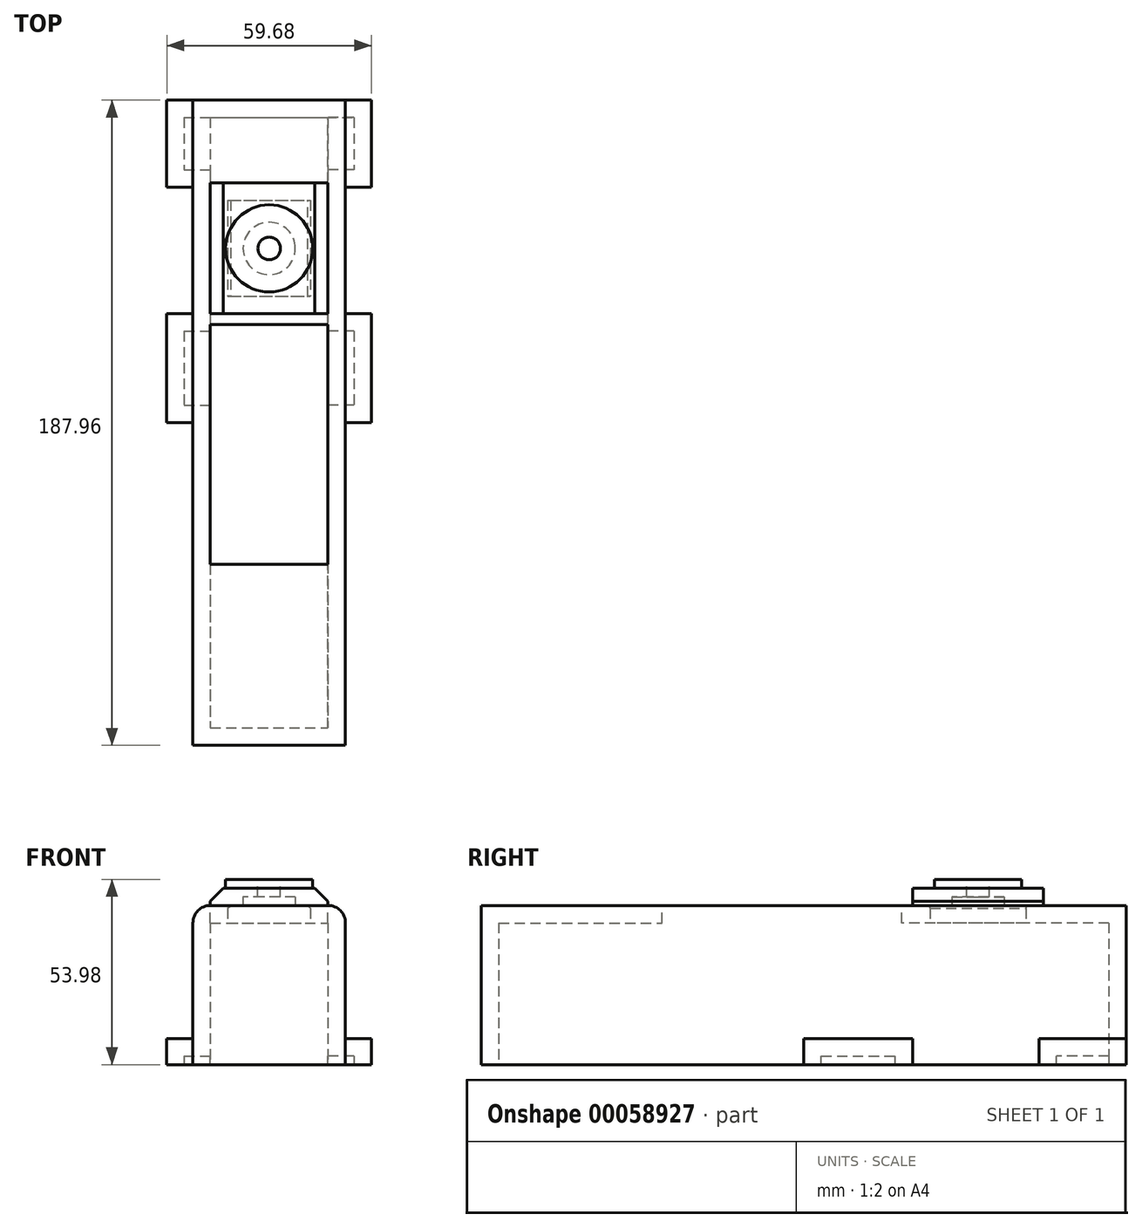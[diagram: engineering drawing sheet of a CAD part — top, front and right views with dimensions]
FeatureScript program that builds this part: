
annotation { "Feature Type Name" : "Feature", "Feature Type Description" : "" }
export const myFeature = defineFeature(function(context is Context, id is Id, definition is map)
    precondition{}
    {
        {
            var Q0;
            Q0=qCreatedBy(makeId("Top.planeOp"),FACE);
            var sketch = newSketch(context, id + "F0", { "sketchPlane" : qUnion([Q0])});
            skLineSegment(sketch, "E0.rect.bottom", {"start": v(-22.22, 93.98) * mm, "end": v(22.22, 93.98) * mm});
            skLineSegment(sketch, "E0.rect.top", {"start": v(-22.22, -93.98) * mm, "end": v(22.22, -93.98) * mm});
            skLineSegment(sketch, "E0.rect.left", {"start": v(-22.22, 93.98) * mm, "end": v(-22.22, -93.98) * mm});
            skLineSegment(sketch, "E0.rect.right", {"start": v(22.22, 93.98) * mm, "end": v(22.22, -93.98) * mm});
            skPoint(sketch, "E0.rect.middle", {"position": v(0, 0) * mm});
            skSolve(sketch);
        }
        {
            var Q0;
            Q0=makeQuery(id+"F0.imprint","IMPRINT",FACE,{"disambiguationData":[TD([[makeQuery(id+"F0.imprint","IMPRINT",EDGE,{"derivedFrom":sQuery(id+"F0.wireOp",EDGE,"E0.rect.bottom")}),-1.0]])]});
            extrude(context, id + "F1", {"entities" : qUnion([Q0]), "depth" : 46.35 * mm});
        }
        {
            var Q0;
            Q0=makeQuery(id+"F1.opExtrude","CAP_EDGE",EDGE,{"disambiguationData":[OSD([sQuery(id+"F0.wireOp",EDGE,"E0.rect.right")])],"isStart":false});
            var Q1;
            Q1=makeQuery(id+"F1.opExtrude","CAP_EDGE",EDGE,{"disambiguationData":[OSD([sQuery(id+"F0.wireOp",EDGE,"E0.rect.left")])],"isStart":false});
            fillet(context, id + "F2", {"entities" : qUnion([Q0, Q1]), "radius" : 5.08 * mm, "tangentPropagation" : true, "allowEdgeOverflow" : false});
        }
        {
            var Q0;
            Q0=makeQuery(id+"F1.opExtrude","CAP_FACE",FACE,{"disambiguationData":[OSD([sQuery(id+"F0.wireOp",EDGE,"E0.rect.bottom"),sQuery(id+"F0.wireOp",EDGE,"E0.rect.top"),sQuery(id+"F0.wireOp",EDGE,"E0.rect.left"),sQuery(id+"F0.wireOp",EDGE,"E0.rect.right")])],"isStart":false});
            var sketch = newSketch(context, id + "F3", { "sketchPlane" : qUnion([Q0])});
            skLineSegment(sketch, "E1.bottom", {"start": v(-17.14, 69.85) * mm, "end": v(17.14, 69.85) * mm});
            skLineSegment(sketch, "E1.top", {"start": v(-17.14, 31.75) * mm, "end": v(17.14, 31.75) * mm});
            skLineSegment(sketch, "E1.left", {"start": v(-17.14, 69.85) * mm, "end": v(-17.14, 31.75) * mm});
            skLineSegment(sketch, "E1.right", {"start": v(17.14, 69.85) * mm, "end": v(17.14, 31.75) * mm});
            skPoint(sketch, "E1.middle", {"position": v(0, 50.8) * mm});
            skSolve(sketch);
        }
        {
            var Q0;
            Q0=makeQuery(id+"F3.imprint","IMPRINT",FACE,{"disambiguationData":[TD([[makeQuery(id+"F3.imprint","IMPRINT",EDGE,{"derivedFrom":sQuery(id+"F3.wireOp",EDGE,"E1.bottom")}),-1.0]])]});
            extrude(context, id + "F4", {"entities" : qUnion([Q0]), "operationType" : NewBodyOperationType.ADD, "depth" : 5.08 * mm});
        }
        {
            var Q0;
            Q0=makeQuery(id+"F4.opExtrude","CAP_FACE",FACE,{"disambiguationData":[OSD([sQuery(id+"F3.wireOp",EDGE,"E1.bottom"),sQuery(id+"F3.wireOp",EDGE,"E1.top"),sQuery(id+"F3.wireOp",EDGE,"E1.left"),sQuery(id+"F3.wireOp",EDGE,"E1.right")])],"isStart":false});
            var sketch = newSketch(context, id + "F5", { "sketchPlane" : qUnion([Q0])});
            skCircle(sketch, "E2", {"center": v(0, 50.8) * mm, "radius": 12.7 * mm});
            skPoint(sketch, "E2.centerSnap0", {"position": v(-17.14, 50.8) * mm});
            skSolve(sketch);
        }
        {
            var Q0;
            Q0=makeQuery(id+"F5.imprint","IMPRINT",FACE,{"disambiguationData":[TD([[makeQuery(id+"F5.imprint","IMPRINT",EDGE,{"derivedFrom":sQuery(id+"F5.wireOp",EDGE,"E2")}),1.0]])]});
            extrude(context, id + "F6", {"entities" : qUnion([Q0]), "operationType" : NewBodyOperationType.ADD, "depth" : 2.54 * mm});
        }
        {
            var Q0;
            Q0=makeQuery(id+"F1.opExtrude","SWEPT_FACE",FACE,{"disambiguationData":[OSD([sQuery(id+"F0.wireOp",EDGE,"E0.rect.right")])]});
            var sketch = newSketch(context, id + "F7", { "sketchPlane" : qUnion([Q0])});
            skLineSegment(sketch, "E3.bottom", {"start": v(0, 0) * mm, "end": v(31.75, 0) * mm});
            skLineSegment(sketch, "E3.top", {"start": v(0, 7.62) * mm, "end": v(31.75, 7.62) * mm});
            skLineSegment(sketch, "E3.left", {"start": v(0, 0) * mm, "end": v(0, 7.62) * mm});
            skLineSegment(sketch, "E3.right", {"start": v(31.75, 0) * mm, "end": v(31.75, 7.62) * mm});
            skSolve(sketch);
        }
        {
            var Q0;
            Q0=makeQuery(id+"F7.imprint","IMPRINT",FACE,{"disambiguationData":[TD([[makeQuery(id+"F7.imprint","IMPRINT",EDGE,{"derivedFrom":sQuery(id+"F7.wireOp",EDGE,"E3.bottom")}),-1.0]])]});
            extrude(context, id + "F8", {"entities" : qUnion([Q0]), "operationType" : NewBodyOperationType.ADD, "depth" : 7.62 * mm});
        }
        {
            var Q0;
            Q0=makeQuery(id+"F1.opExtrude","SWEPT_FACE",FACE,{"disambiguationData":[OSD([sQuery(id+"F0.wireOp",EDGE,"E0.rect.left")])]});
            var sketch = newSketch(context, id + "F9", { "sketchPlane" : qUnion([Q0])});
            skLineSegment(sketch, "E4.bottom", {"start": v(0, 0) * mm, "end": v(-31.75, 0) * mm});
            skLineSegment(sketch, "E4.top", {"start": v(0, 7.62) * mm, "end": v(-31.75, 7.62) * mm});
            skLineSegment(sketch, "E4.left", {"start": v(0, 0) * mm, "end": v(0, 7.62) * mm});
            skLineSegment(sketch, "E4.right", {"start": v(-31.75, 0) * mm, "end": v(-31.75, 7.62) * mm});
            skSolve(sketch);
        }
        {
            var Q0;
            Q0=makeQuery(id+"F9.imprint","IMPRINT",FACE,{"disambiguationData":[TD([[makeQuery(id+"F9.imprint","IMPRINT",EDGE,{"derivedFrom":sQuery(id+"F9.wireOp",EDGE,"E4.bottom")}),1.0]])]});
            extrude(context, id + "F10", {"entities" : qUnion([Q0]), "operationType" : NewBodyOperationType.ADD, "depth" : 7.62 * mm});
        }
        {
            var Q0;
            Q0=makeQuery(id+"F1.opExtrude","SWEPT_FACE",FACE,{"disambiguationData":[OSD([sQuery(id+"F0.wireOp",EDGE,"E0.rect.left")])]});
            var sketch = newSketch(context, id + "F11", { "sketchPlane" : qUnion([Q0])});
            skLineSegment(sketch, "E5.bottom", {"start": v(-93.98, 0) * mm, "end": v(-68.58, 0) * mm});
            skLineSegment(sketch, "E5.top", {"start": v(-93.98, 7.62) * mm, "end": v(-68.58, 7.62) * mm});
            skLineSegment(sketch, "E5.left", {"start": v(-93.98, 0) * mm, "end": v(-93.98, 7.62) * mm});
            skLineSegment(sketch, "E5.right", {"start": v(-68.58, 0) * mm, "end": v(-68.58, 7.62) * mm});
            skSolve(sketch);
        }
        {
            var Q0;
            Q0=makeQuery(id+"F11.imprint","IMPRINT",FACE,{"disambiguationData":[TD([[makeQuery(id+"F11.imprint","IMPRINT",EDGE,{"derivedFrom":sQuery(id+"F11.wireOp",EDGE,"E5.bottom")}),1.0]])]});
            extrude(context, id + "F12", {"entities" : qUnion([Q0]), "operationType" : NewBodyOperationType.ADD, "depth" : 7.62 * mm});
        }
        {
            var Q0;
            Q0=makeQuery(id+"F1.opExtrude","SWEPT_FACE",FACE,{"disambiguationData":[OSD([sQuery(id+"F0.wireOp",EDGE,"E0.rect.right")])]});
            var sketch = newSketch(context, id + "F13", { "sketchPlane" : qUnion([Q0])});
            skLineSegment(sketch, "E6.bottom", {"start": v(93.98, 0) * mm, "end": v(68.58, 0) * mm});
            skLineSegment(sketch, "E6.top", {"start": v(93.98, 7.62) * mm, "end": v(68.58, 7.62) * mm});
            skLineSegment(sketch, "E6.left", {"start": v(93.98, 0) * mm, "end": v(93.98, 7.62) * mm});
            skLineSegment(sketch, "E6.right", {"start": v(68.58, 0) * mm, "end": v(68.58, 7.62) * mm});
            skSolve(sketch);
        }
        {
            var Q0;
            Q0=makeQuery(id+"F13.imprint","IMPRINT",FACE,{"disambiguationData":[TD([[makeQuery(id+"F13.imprint","IMPRINT",EDGE,{"derivedFrom":sQuery(id+"F13.wireOp",EDGE,"E6.bottom")}),-1.0]])]});
            extrude(context, id + "F14", {"entities" : qUnion([Q0]), "operationType" : NewBodyOperationType.ADD, "depth" : 7.62 * mm});
        }
        {
            var Q0;
            Q0=makeQuery(id+"F4.opExtrude","CAP_EDGE",EDGE,{"disambiguationData":[OSD([sQuery(id+"F3.wireOp",EDGE,"E1.left")])],"isStart":false});
            var Q1;
            Q1=makeQuery(id+"F4.opExtrude","CAP_EDGE",EDGE,{"disambiguationData":[OSD([sQuery(id+"F3.wireOp",EDGE,"E1.right")])],"isStart":false});
            chamfer(context, id + "F15", {"entities" : qUnion([Q0, Q1]), "width" : 3.8 * mm, "tangentPropagation" : true});
        }
        {
            var Q0;
            Q0=makeQuery(id+"F14.boolean.opBoolean","MERGE",FACE,{"derivedFrom":[makeQuery(id+"F12.boolean.opBoolean","MERGE",FACE,{"derivedFrom":[makeQuery(id+"F10.boolean.opBoolean","MERGE",FACE,{"derivedFrom":[makeQuery(id+"F8.boolean.opBoolean","MERGE",FACE,{"derivedFrom":[makeQuery(id+"F1.opExtrude","CAP_FACE",FACE,{"disambiguationData":[OSD([sQuery(id+"F0.wireOp",EDGE,"E0.rect.bottom"),sQuery(id+"F0.wireOp",EDGE,"E0.rect.top"),sQuery(id+"F0.wireOp",EDGE,"E0.rect.left"),sQuery(id+"F0.wireOp",EDGE,"E0.rect.right")])],"isStart":true}),makeQuery(id+"F8.opExtrude","SWEPT_FACE",FACE,{"disambiguationData":[OSD([sQuery(id+"F7.wireOp",EDGE,"E3.bottom")])]})]}),makeQuery(id+"F10.opExtrude","SWEPT_FACE",FACE,{"disambiguationData":[OSD([sQuery(id+"F9.wireOp",EDGE,"E4.bottom")])]})]}),makeQuery(id+"F12.opExtrude","SWEPT_FACE",FACE,{"disambiguationData":[OSD([sQuery(id+"F11.wireOp",EDGE,"E5.bottom")])]})]}),makeQuery(id+"F14.opExtrude","SWEPT_FACE",FACE,{"disambiguationData":[OSD([sQuery(id+"F13.wireOp",EDGE,"E6.bottom")])]})]});
            shell(context, id + "F16", {"entities" : qUnion([Q0]), "thickness" : 5.08 * mm});
        }
        {
            var Q0;
            {var subQ0=sQuery(id+"F0.wireOp",EDGE,"E0.rect.left");var subQ1=sQuery(id+"F0.wireOp",EDGE,"E0.rect.right");var subQ2=sQuery(id+"F0.wireOp",EDGE,"E0.rect.top");Q0=makeQuery(id+"F4.boolean.opBoolean","SPLIT",FACE,{"disambiguationData":[TD([makeQuery(id+"F1.opExtrude","SWEPT_FACE",FACE,{"disambiguationData":[OSD([subQ2])]})])],"derivedFrom":makeQuery(id+"F1.opExtrude","CAP_FACE",FACE,{"disambiguationData":[OSD([sQuery(id+"F0.wireOp",EDGE,"E0.rect.bottom"),subQ2,subQ0,subQ1])],"isStart":false})});}
            var sketch = newSketch(context, id + "F17", { "sketchPlane" : qUnion([Q0])});
            skLineSegment(sketch, "E7.bottom", {"start": v(-17.14, 28.58) * mm, "end": v(17.14, 28.58) * mm});
            skLineSegment(sketch, "E7.top", {"start": v(-17.14, -41.28) * mm, "end": v(17.14, -41.28) * mm});
            skLineSegment(sketch, "E7.left", {"start": v(-17.14, 28.58) * mm, "end": v(-17.14, -41.28) * mm});
            skLineSegment(sketch, "E7.right", {"start": v(17.14, 28.58) * mm, "end": v(17.14, -41.28) * mm});
            skSolve(sketch);
        }
        {
            var Q0;
            Q0=makeQuery(id+"F17.imprint","IMPRINT",FACE,{"disambiguationData":[TD([[makeQuery(id+"F17.imprint","IMPRINT",EDGE,{"derivedFrom":sQuery(id+"F17.wireOp",EDGE,"E7.bottom")}),-1.0]])]});
            extrude(context, id + "F18", {"entities" : qUnion([Q0]), "operationType" : NewBodyOperationType.REMOVE, "oppositeDirection" : true, "depth" : 25.4 * mm});
        }
        {
            var Q0;
            Q0=makeQuery(id+"F6.opExtrude","CAP_FACE",FACE,{"disambiguationData":[OSD([sQuery(id+"F5.wireOp",EDGE,"E2")])],"isStart":false});
            var sketch = newSketch(context, id + "F19", { "sketchPlane" : qUnion([Q0])});
            skCircle(sketch, "E8", {"center": v(0, 50.8) * mm, "radius": 3.3 * mm});
            skSolve(sketch);
        }
        {
            var Q0;
            Q0=makeQuery(id+"F19.imprint","IMPRINT",FACE,{"disambiguationData":[TD([[makeQuery(id+"F19.imprint","IMPRINT",EDGE,{"derivedFrom":sQuery(id+"F19.wireOp",EDGE,"E8")}),1.0]])]});
            extrude(context, id + "F20", {"entities" : qUnion([Q0]), "operationType" : NewBodyOperationType.REMOVE, "endBound" : BoundingType.THROUGH_ALL, "oppositeDirection" : true, "depth" : 25.4 * mm});
        }
    });
